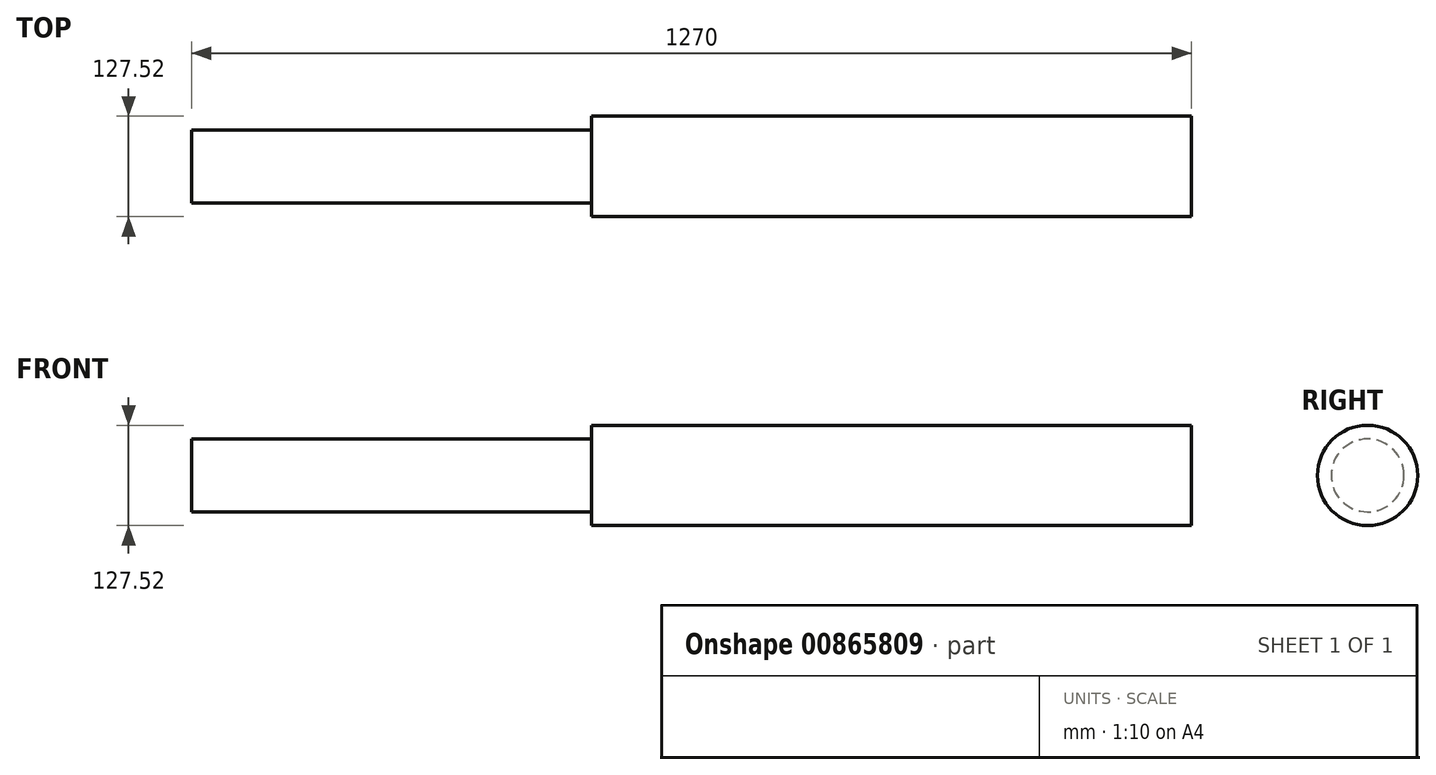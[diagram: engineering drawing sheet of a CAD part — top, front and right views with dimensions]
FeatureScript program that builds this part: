
annotation { "Feature Type Name" : "Feature", "Feature Type Description" : "" }
export const myFeature = defineFeature(function(context is Context, id is Id, definition is map)
    precondition{}
    {
        {
            var Q0;
            Q0=qCreatedBy(makeId("Right.planeOp"),FACE);
            var sketch = newSketch(context, id + "F0", { "sketchPlane" : qUnion([Q0])});
            skCircle(sketch, "E0", {"center": v(0, 0) * mm, "radius": 63.76 * mm});
            skSolve(sketch);
        }
        {
            var Q0;
            Q0=makeQuery(id+"F0.imprint","IMPRINT",FACE,{"disambiguationData":[TD([[makeQuery(id+"F0.imprint","IMPRINT",EDGE,{"derivedFrom":sQuery(id+"F0.wireOp",EDGE,"E0")}),1.0]])]});
            extrude(context, id + "F1", {"entities" : qUnion([Q0]), "depth" : 1270 * mm, "offsetDistance" : 25.4 * mm});
        }
        {
            var Q0;
            Q0=qCreatedBy(makeId("Right.planeOp"),FACE);
            var sketch = newSketch(context, id + "F2", { "sketchPlane" : qUnion([Q0])});
            skCircle(sketch, "E1", {"center": v(0, 0) * mm, "radius": 63.84 * mm});
            skCircle(sketch, "E2", {"center": v(0, 0) * mm, "radius": 46.27 * mm});
            skSolve(sketch);
        }
        {
            var Q0;
            Q0=makeQuery(id+"F2.imprint","IMPRINT",FACE,{"disambiguationData":[TD([[makeQuery(id+"F2.imprint","IMPRINT",EDGE,{"derivedFrom":sQuery(id+"F2.wireOp",EDGE,"E1")}),1.0]])]});
            extrude(context, id + "F3", {"entities" : qUnion([Q0]), "operationType" : NewBodyOperationType.REMOVE, "depth" : 508 * mm, "offsetDistance" : 25.4 * mm});
        }
    });
